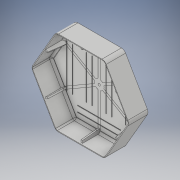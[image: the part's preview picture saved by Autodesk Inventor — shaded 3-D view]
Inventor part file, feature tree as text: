
AUTODESK INVENTOR PART (.ipt)
format: ipt  version: 2019 (Build 230136000, 136)  size: 925,696 bytes
history: native  units: mm
features: projected_geometry x23, sketch x9, extrude x5, plane x3, fillet x3, other x3, shell x1, pattern_circular x1
ambient origin geometry x8: Origin, YZ Plane, XZ Plane, XY Plane, X Axis, Y Axis, Z Axis, Center Point
bodies: Solid1 (feature_tree)
feature tree (48):
  extrude  "Extrusion1"  Depth=40.0mm TaperAngle=0.0deg
  shell  "Shell1"  Thickness=1.5mm
  extrude  "Extrusion9"  Depth=10.0mm
  plane  "Work Plane1"
  plane  "Work Plane2"
  plane  "Work Plane3"
  sketch  "Sketch12"  dims[d55=5.0mm]
  extrude  "Extrusion5"  Depth=5.0mm
  extrude  "Extrusion6"  TaperAngle=60.0deg  [1 undecoded]
  extrude  "Extrusion8"  TaperAngle=90.0deg  [1 undecoded]
  pattern_circular  "Circular Pattern1"  [2 undecoded]
  fillet  "Fillet1"  Radius=8.0mm
  fillet  "Fillet2"  Radius=36.0mm
  fillet  "Fillet4"  Radius=60.0mm
  sketch  "Sketch5"  dims[d12=1.0mm d37=5.0mm]
  sketch  "Sketch6"  dims[d44=10.0mm d45=60.0deg]
  sketch  "Sketch7"  dims[d46=90.0deg d47=90.0deg]
  other  "Work Axis4"
  other  "Work Axis5"
  other  "Work Axis6"
  sketch  "Sketch13"  dims[d56=2.0mm d57=3.0mm d58=8.0mm d59=36.0mm d60=0.0mm d70=60.0mm d72=360.0deg d74=60.0mm d75=360.0deg d77=3.0mm d78=30.0mm d79=20.0mm d80=0.0mm d138=11.0mm d139=87.0mm d140=40.0mm d142=40.5mm d143=10.0mm d145=10.0mm d147=130.0mm d149=0.5mm d150=0.0mm d151=1.0mm d152=1.0mm d153=1.0mm d154=1.0mm d155=1.0mm d156=1.0mm]
  sketch  "Sketch1"  dims[d0=175.0mm d2=40.0mm d3=0.0mm d4=1.5mm]
  sketch  "Sketch4"  dims[d10=4.0mm d11=10.0mm]
  projected_geometry  "Projected Loop3"
  sketch  "Sketch8"  dims[d52=5.5mm]
  projected_geometry  "Projected Loop4"
  sketch  "Sketch9"  dims[d53=0.01mm d54=0.0mm]
  projected_geometry  "Projected Loop5"
  projected_geometry  "Projected Loop6"
  projected_geometry  "Projected Loop7"
  projected_geometry  "Projected Loop8"
  projected_geometry  "Projected Loop9"
  projected_geometry  "Projected Loop10"
  projected_geometry  "Projected Loop11"
  projected_geometry  "Projected Loop12"
  projected_geometry  "Projected Loop13"
  projected_geometry  "Projected Loop14"
  projected_geometry  "Projected Loop15"
  projected_geometry  "Projected Loop16"
  projected_geometry  "Projected Loop17"
  projected_geometry  "Projected Loop18"
  projected_geometry  "Projected Loop19"
  projected_geometry  "Projected Loop20"
  projected_geometry  "Projected Loop21"
  projected_geometry  "Projected Loop22"
  projected_geometry  "Projected Loop23"
  projected_geometry  "Projected Loop24"
  projected_geometry  "Projected Loop25"
note: 4 required parameter values undecoded (feature->parameter linkage not recoverable at this tier; creation-order binding heuristic only, values carry confidence <= 0.55)
